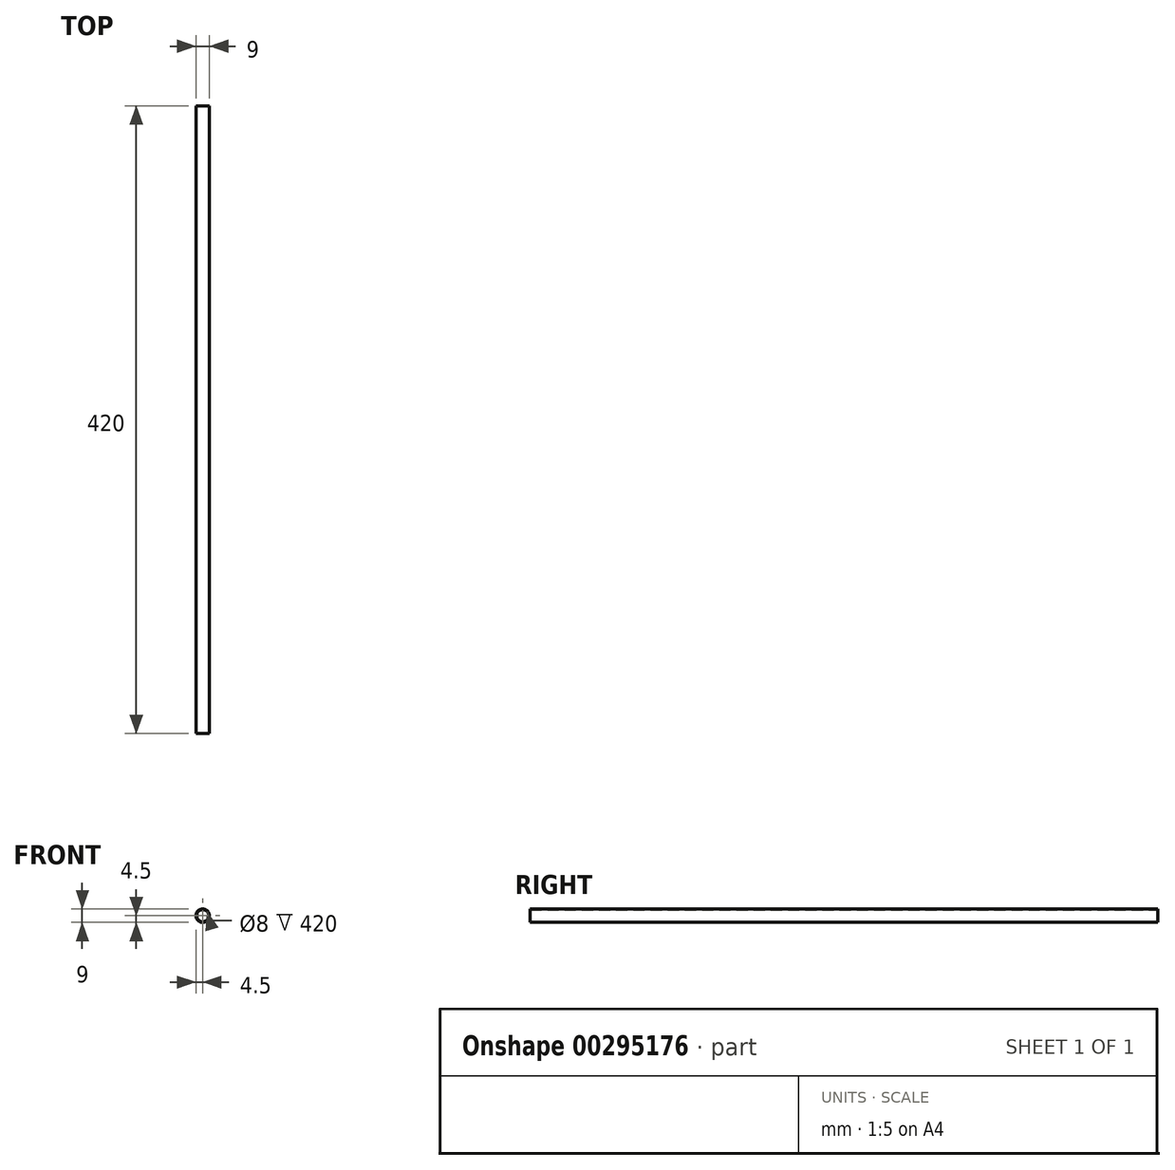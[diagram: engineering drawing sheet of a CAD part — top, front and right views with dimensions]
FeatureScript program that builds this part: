
annotation { "Feature Type Name" : "Feature", "Feature Type Description" : "" }
export const myFeature = defineFeature(function(context is Context, id is Id, definition is map)
    precondition{}
    {
        {
            var Q0;
            Q0=qCreatedBy(makeId("Front.planeOp"),FACE);
            var sketch = newSketch(context, id + "F0", { "sketchPlane" : qUnion([Q0])});
            skCircle(sketch, "E0", {"center": v(0, 0) * mm, "radius": 4.5 * mm});
            skCircle(sketch, "E1", {"center": v(0, 0) * mm, "radius": 4 * mm});
            skSolve(sketch);
        }
        {
            var Q0;
            Q0=makeQuery(id+"F0.imprint","IMPRINT",FACE,{"disambiguationData":[TD([[makeQuery(id+"F0.imprint","IMPRINT",EDGE,{"derivedFrom":sQuery(id+"F0.wireOp",EDGE,"E0")}),1.0]])]});
            extrude(context, id + "F1", {"entities" : qUnion([Q0]), "endBound" : BoundingType.SYMMETRIC, "depth" : 420 * mm});
        }
    });
